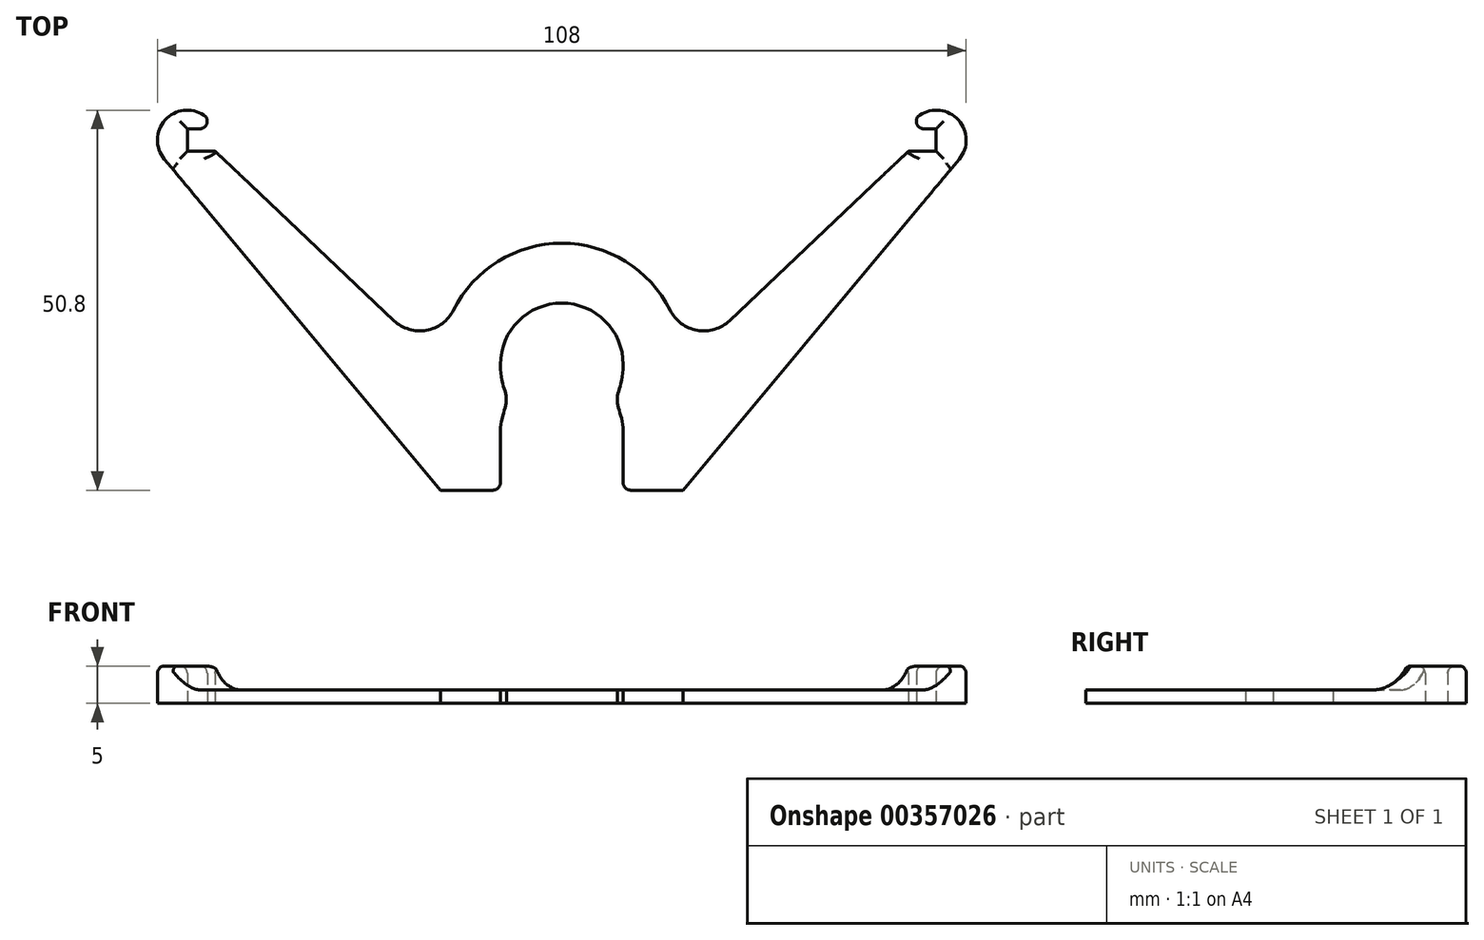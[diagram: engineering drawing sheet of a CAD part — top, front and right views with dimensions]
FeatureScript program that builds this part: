
annotation { "Feature Type Name" : "Feature", "Feature Type Description" : "" }
export const myFeature = defineFeature(function(context is Context, id is Id, definition is map)
    precondition{}
    {
        {
            var Q0;
            Q0=qCreatedBy(makeId("Top.planeOp"),FACE);
            var sketch = newSketch(context, id + "F0", { "sketchPlane" : qUnion([Q0])});
            skArc(sketch, "E0", {"start": v(8.2, 0) * mm, "mid": v(0, 8.2) * mm, "end": v(-8.2, 0) * mm});
            skLineSegment(sketch, "E1.bottom", {"start": v(-8.2, 0) * mm, "end": v(8.2, 0) * mm});
            skLineSegment(sketch, "E1.top", {"start": v(-8.2, -16.8) * mm, "end": v(8.2, -16.8) * mm});
            skLineSegment(sketch, "E1.left", {"start": v(-8.2, 0) * mm, "end": v(-8.2, -16.8) * mm});
            skLineSegment(sketch, "E1.right", {"start": v(8.2, 0) * mm, "end": v(8.2, -16.8) * mm});
            skPoint(sketch, "E1.middle", {"position": v(0, -8.4) * mm});
            skLineSegment(sketch, "E2.0", {"start": v(-7.4, 0) * mm, "end": v(-7.4, -16.8) * mm, "construction": true});
            skFitSpline(sketch, "E3", {"points": [v(-8.2, 0) * mm, v(-7.4, -4.8) * mm, v(-8.2, -8.87) * mm], "startDerivative": vector(0, -14.7) * mm, "endDerivative": vector(0, -10.25) * mm});
            skFitSpline(sketch, "E4.MirrorCS", {"points": [v(8.2, 0) * mm, v(7.4, -4.8) * mm, v(8.2, -8.87) * mm], "startDerivative": vector(0, -14.7) * mm, "endDerivative": vector(0, -10.25) * mm});
            skLineSegment(sketch, "E5.0", {"start": v(-16.2, 0) * mm, "end": v(-16.2, -16.8) * mm});
            skArc(sketch, "E5.1", {"start": v(16.2, 0) * mm, "mid": v(0, 16.2) * mm, "end": v(-16.2, 0) * mm});
            skLineSegment(sketch, "E5.2", {"start": v(16.2, 0) * mm, "end": v(16.2, -16.8) * mm});
            skLineSegment(sketch, "E6", {"start": v(16.2, -16.8) * mm, "end": v(8.2, -16.8) * mm});
            skLineSegment(sketch, "E7", {"start": v(-8.2, -16.8) * mm, "end": v(-16.2, -16.8) * mm});
            skLineSegment(sketch, "E8.bottom", {"start": v(50, 28.5) * mm, "end": v(46.3, 28.5) * mm});
            skLineSegment(sketch, "E8.top", {"start": v(50, 31.5) * mm, "end": v(48.34, 31.5) * mm});
            skLineSegment(sketch, "E8.left", {"start": v(50, 28.5) * mm, "end": v(50, 31.5) * mm});
            skLineSegment(sketch, "E8.right", {"start": v(-50, 28.5) * mm, "end": v(-50, 31.5) * mm});
            skPoint(sketch, "E8.middle", {"position": v(0, 30) * mm});
            skArc(sketch, "E9", {"start": v(46.3, 28.5) * mm, "mid": v(53.82, 28.82) * mm, "end": v(47.79, 33.33) * mm});
            skLineSegment(sketch, "E10", {"start": v(53.07, 27.44) * mm, "end": v(16.2, -16.8) * mm});
            skLineSegment(sketch, "E11.MirrorCS", {"start": v(-53.07, 27.44) * mm, "end": v(-16.2, -16.8) * mm});
            skLineSegment(sketch, "E12.trimOffspring", {"start": v(-46.3, 31.5) * mm, "end": v(-50, 31.5) * mm});
            skPoint(sketch, "E13.visualSharp", {"position": v(46.3, 31.5) * mm});
            skArc(sketch, "E13.filletArc", {"start": v(47.79, 33.33) * mm, "mid": v(47.38, 32.21) * mm, "end": v(48.34, 31.5) * mm});
            skArc(sketch, "E14.MirrorCS", {"start": v(-46.3, 28.5) * mm, "mid": v(-53.82, 28.82) * mm, "end": v(-47.79, 33.33) * mm});
            skArc(sketch, "E15.MirrorCS", {"start": v(-47.79, 33.33) * mm, "mid": v(-47.38, 32.21) * mm, "end": v(-48.34, 31.5) * mm});
            skLineSegment(sketch, "E16", {"start": v(46.3, 28.5) * mm, "end": v(16.2, 0) * mm});
            skLineSegment(sketch, "E17.MirrorCS", {"start": v(-46.3, 28.5) * mm, "end": v(-16.2, 0) * mm});
            skLineSegment(sketch, "E18.trimOffspring", {"start": v(-46.3, 28.5) * mm, "end": v(-50, 28.5) * mm});
            skSolve(sketch);
        }
        {
            var Q0;
            {var subQ6=sQuery(id+"F0.wireOp",EDGE,"E0");Q0=makeQuery(id+"F0.imprint","IMPRINT",FACE,{"disambiguationData":[TD([[makeQuery(id+"F0.imprint","IMPRINT",EDGE,{"derivedFrom":subQ6}),-1.0]])]});}
            var Q1;
            {var subQ0=sQuery(id+"F0.wireOp",EDGE,"E4.MirrorCS");Q1=makeQuery(id+"F0.imprint","IMPRINT",FACE,{"disambiguationData":[TD([[makeQuery(id+"F0.imprint","IMPRINT",EDGE,{"derivedFrom":subQ0}),1.0]])]});}
            var Q2;
            {var subQ0=sQuery(id+"F0.wireOp",EDGE,"E3");Q2=makeQuery(id+"F0.imprint","IMPRINT",FACE,{"disambiguationData":[TD([[makeQuery(id+"F0.imprint","IMPRINT",EDGE,{"derivedFrom":subQ0}),-1.0]])]});}
            var Q3;
            {var subQ0=sQuery(id+"F0.wireOp",EDGE,"E10");Q3=makeQuery(id+"F0.imprint","IMPRINT",FACE,{"disambiguationData":[TD([[makeQuery(id+"F0.imprint","IMPRINT",EDGE,{"derivedFrom":subQ0}),-1.0]])]});}
            var Q4;
            Q4=makeQuery(id+"F0.imprint","IMPRINT",FACE,{"disambiguationData":[TD([[makeQuery(id+"F0.imprint","IMPRINT",EDGE,{"derivedFrom":sQuery(id+"F0.wireOp",EDGE,"E8.top")}),-1.0]])]});
            var Q5;
            {var subQ1=sQuery(id+"F0.wireOp",EDGE,"E8.right");Q5=makeQuery(id+"F0.imprint","IMPRINT",FACE,{"disambiguationData":[TD([[makeQuery(id+"F0.imprint","IMPRINT",EDGE,{"derivedFrom":subQ1}),1.0]])]});}
            var Q6;
            Q6=makeQuery(id+"F0.imprint","IMPRINT",FACE,{"disambiguationData":[TD([[makeQuery(id+"F0.imprint","IMPRINT",EDGE,{"derivedFrom":sQuery(id+"F0.wireOp",EDGE,"E5.0")}),-1.0]])]});
            extrude(context, id + "F1", {"entities" : qUnion([Q0, Q1, Q2, Q3, Q4, Q5, Q6]), "depth" : 1.8 * mm});
        }
        {
            var Q0;
            Q0=makeQuery(id+"F1.opExtrude","SWEPT_EDGE",EDGE,{"disambiguationData":[OSD([sQuery(id+"F0.wireOp",EDGE,"E1.top"),sQuery(id+"F0.wireOp",EDGE,"E1.left"),sQuery(id+"F0.wireOp",EDGE,"E7")])]});
            var Q1;
            Q1=makeQuery(id+"F1.opExtrude","SWEPT_EDGE",EDGE,{"disambiguationData":[OSD([sQuery(id+"F0.wireOp",EDGE,"E1.top"),sQuery(id+"F0.wireOp",EDGE,"E1.right"),sQuery(id+"F0.wireOp",EDGE,"E6")])]});
            fillet(context, id + "F2", {"entities" : qUnion([Q0, Q1]), "radius" : 1 * mm, "tangentPropagation" : true, "allowEdgeOverflow" : false});
        }
        {
            var Q0;
            Q0=makeQuery(id+"F0.imprint","IMPRINT",FACE,{"disambiguationData":[TD([[makeQuery(id+"F0.imprint","IMPRINT",EDGE,{"derivedFrom":sQuery(id+"F0.wireOp",EDGE,"E8.top")}),-1.0]])]});
            var Q1;
            {var subQ1=sQuery(id+"F0.wireOp",EDGE,"E8.right");Q1=makeQuery(id+"F0.imprint","IMPRINT",FACE,{"disambiguationData":[TD([[makeQuery(id+"F0.imprint","IMPRINT",EDGE,{"derivedFrom":subQ1}),1.0]])]});}
            extrude(context, id + "F3", {"entities" : qUnion([Q0, Q1]), "operationType" : NewBodyOperationType.ADD, "depth" : 5 * mm});
        }
        {
            var Q0;
            {var subQ0=sQuery(id+"F0.wireOp",EDGE,"E9");Q0=makeQuery(id+"F3.boolean.opBoolean","INTERSECT",EDGE,{"derivedFrom":[makeQuery(id+"F1.opExtrude","CAP_FACE",FACE,{"disambiguationData":[OSD([sQuery(id+"F0.wireOp",EDGE,"E0"),sQuery(id+"F0.wireOp",EDGE,"E1.left"),sQuery(id+"F0.wireOp",EDGE,"E1.right"),sQuery(id+"F0.wireOp",EDGE,"E3"),sQuery(id+"F0.wireOp",EDGE,"E4.MirrorCS"),sQuery(id+"F0.wireOp",EDGE,"E5.1"),sQuery(id+"F0.wireOp",EDGE,"E6"),sQuery(id+"F0.wireOp",EDGE,"E7"),sQuery(id+"F0.wireOp",EDGE,"E8.bottom"),sQuery(id+"F0.wireOp",EDGE,"E8.top"),sQuery(id+"F0.wireOp",EDGE,"E8.left"),sQuery(id+"F0.wireOp",EDGE,"E8.right"),subQ0,sQuery(id+"F0.wireOp",EDGE,"E10"),sQuery(id+"F0.wireOp",EDGE,"E11.MirrorCS"),sQuery(id+"F0.wireOp",EDGE,"E12.trimOffspring"),sQuery(id+"F0.wireOp",EDGE,"E13.filletArc"),sQuery(id+"F0.wireOp",EDGE,"E14.MirrorCS"),sQuery(id+"F0.wireOp",EDGE,"E15.MirrorCS"),sQuery(id+"F0.wireOp",EDGE,"E16"),sQuery(id+"F0.wireOp",EDGE,"E17.MirrorCS"),sQuery(id+"F0.wireOp",EDGE,"E18.trimOffspring")])],"isStart":false}),makeQuery(id+"F3.opExtrude","SWEPT_FACE",FACE,{"disambiguationData":[OSD([subQ0])]})]});}
            var Q1;
            {var subQ0=sQuery(id+"F0.wireOp",EDGE,"E14.MirrorCS");Q1=makeQuery(id+"F3.boolean.opBoolean","INTERSECT",EDGE,{"derivedFrom":[makeQuery(id+"F1.opExtrude","CAP_FACE",FACE,{"disambiguationData":[OSD([sQuery(id+"F0.wireOp",EDGE,"E0"),sQuery(id+"F0.wireOp",EDGE,"E1.left"),sQuery(id+"F0.wireOp",EDGE,"E1.right"),sQuery(id+"F0.wireOp",EDGE,"E3"),sQuery(id+"F0.wireOp",EDGE,"E4.MirrorCS"),sQuery(id+"F0.wireOp",EDGE,"E5.1"),sQuery(id+"F0.wireOp",EDGE,"E6"),sQuery(id+"F0.wireOp",EDGE,"E7"),sQuery(id+"F0.wireOp",EDGE,"E8.bottom"),sQuery(id+"F0.wireOp",EDGE,"E8.top"),sQuery(id+"F0.wireOp",EDGE,"E8.left"),sQuery(id+"F0.wireOp",EDGE,"E8.right"),sQuery(id+"F0.wireOp",EDGE,"E9"),sQuery(id+"F0.wireOp",EDGE,"E10"),sQuery(id+"F0.wireOp",EDGE,"E11.MirrorCS"),sQuery(id+"F0.wireOp",EDGE,"E12.trimOffspring"),sQuery(id+"F0.wireOp",EDGE,"E13.filletArc"),subQ0,sQuery(id+"F0.wireOp",EDGE,"E15.MirrorCS"),sQuery(id+"F0.wireOp",EDGE,"E16"),sQuery(id+"F0.wireOp",EDGE,"E17.MirrorCS"),sQuery(id+"F0.wireOp",EDGE,"E18.trimOffspring")])],"isStart":false}),makeQuery(id+"F3.opExtrude","SWEPT_FACE",FACE,{"disambiguationData":[OSD([subQ0])]})]});}
            var Q2;
            Q2=makeQuery(id+"F1.opExtrude","SWEPT_EDGE",EDGE,{"disambiguationData":[OSD([sQuery(id+"F0.wireOp",EDGE,"E5.1"),sQuery(id+"F0.wireOp",EDGE,"E5.2"),sQuery(id+"F0.wireOp",EDGE,"E16")])]});
            var Q3;
            Q3=makeQuery(id+"F1.opExtrude","SWEPT_EDGE",EDGE,{"disambiguationData":[OSD([sQuery(id+"F0.wireOp",EDGE,"E5.0"),sQuery(id+"F0.wireOp",EDGE,"E5.1"),sQuery(id+"F0.wireOp",EDGE,"E17.MirrorCS")])]});
            fillet(context, id + "F4", {"entities" : qUnion([Q0, Q1, Q2, Q3]), "radius" : 5 * mm, "tangentPropagation" : true, "allowEdgeOverflow" : false});
        }
        {
            var Q0;
            Q0=makeQuery(id+"F3.opExtrude","CAP_FACE",FACE,{"disambiguationData":[OSD([sQuery(id+"F0.wireOp",EDGE,"E8.bottom"),sQuery(id+"F0.wireOp",EDGE,"E8.top"),sQuery(id+"F0.wireOp",EDGE,"E8.left"),sQuery(id+"F0.wireOp",EDGE,"E9"),sQuery(id+"F0.wireOp",EDGE,"E13.filletArc")])],"isStart":false});
            var Q1;
            {var subQ0=sQuery(id+"F0.wireOp",EDGE,"E8.right");var subQ1=sQuery(id+"F0.wireOp",EDGE,"E8.bottom");var subQ2=sQuery(id+"F0.wireOp",EDGE,"E14.MirrorCS");var subQ3=sQuery(id+"F0.wireOp",EDGE,"E8.left");var subQ4=sQuery(id+"F0.wireOp",EDGE,"E9");Q1=makeQuery(id+"F4.opFillet","BLEND_EDGE",EDGE,{"blendedFrom":[makeQuery(id+"F3.boolean.opBoolean","INTERSECT",EDGE,{"derivedFrom":[makeQuery(id+"F1.opExtrude","CAP_FACE",FACE,{"disambiguationData":[OSD([sQuery(id+"F0.wireOp",EDGE,"E0"),sQuery(id+"F0.wireOp",EDGE,"E1.left"),sQuery(id+"F0.wireOp",EDGE,"E1.right"),sQuery(id+"F0.wireOp",EDGE,"E3"),sQuery(id+"F0.wireOp",EDGE,"E4.MirrorCS"),sQuery(id+"F0.wireOp",EDGE,"E5.0"),sQuery(id+"F0.wireOp",EDGE,"E5.1"),sQuery(id+"F0.wireOp",EDGE,"E5.2"),sQuery(id+"F0.wireOp",EDGE,"E6"),sQuery(id+"F0.wireOp",EDGE,"E7"),subQ1,sQuery(id+"F0.wireOp",EDGE,"E8.top"),subQ3,subQ0,subQ4,sQuery(id+"F0.wireOp",EDGE,"E10"),sQuery(id+"F0.wireOp",EDGE,"E11.MirrorCS"),sQuery(id+"F0.wireOp",EDGE,"E12.trimOffspring"),sQuery(id+"F0.wireOp",EDGE,"E13.filletArc"),subQ2,sQuery(id+"F0.wireOp",EDGE,"E15.MirrorCS")])],"isStart":false}),makeQuery(id+"F3.opExtrude","SWEPT_FACE",FACE,{"disambiguationData":[OSD([subQ4])]})]}),makeQuery(id+"F3.boolean.opBoolean","MERGE",FACE,{"derivedFrom":[makeQuery(id+"F1.opExtrude","SWEPT_FACE",FACE,{"disambiguationData":[OSD([subQ1])]}),makeQuery(id+"F3.opExtrude","SWEPT_FACE",FACE,{"disambiguationData":[OSD([subQ1]),TDD([makeQuery(id+"F0.imprint","IMPRINT",EDGE,{"disambiguationData":[TD([[makeQuery(id+"F0.imprint","INTERSECT",VERTEX,{"derivedFrom":[subQ1,subQ3]}),-1.0]])],"derivedFrom":subQ1})])]}),makeQuery(id+"F3.opExtrude","SWEPT_FACE",FACE,{"disambiguationData":[OSD([subQ1]),TDD([makeQuery(id+"F0.imprint","IMPRINT",EDGE,{"disambiguationData":[TD([[makeQuery(id+"F0.imprint","INTERSECT",VERTEX,{"derivedFrom":[subQ1,subQ0]}),1.0]])],"derivedFrom":subQ1})])]})]})],"blendedInto":[makeQuery(id+"F3.boolean.opBoolean","MERGE",FACE,{"derivedFrom":[makeQuery(id+"F1.opExtrude","SWEPT_FACE",FACE,{"disambiguationData":[OSD([subQ1])]}),makeQuery(id+"F3.opExtrude","SWEPT_FACE",FACE,{"disambiguationData":[OSD([subQ1]),TDD([makeQuery(id+"F0.imprint","IMPRINT",EDGE,{"disambiguationData":[TD([[makeQuery(id+"F0.imprint","INTERSECT",VERTEX,{"derivedFrom":[subQ1,subQ3]}),-1.0]])],"derivedFrom":subQ1})])]}),makeQuery(id+"F3.opExtrude","SWEPT_FACE",FACE,{"disambiguationData":[OSD([subQ1]),TDD([makeQuery(id+"F0.imprint","IMPRINT",EDGE,{"disambiguationData":[TD([[makeQuery(id+"F0.imprint","INTERSECT",VERTEX,{"derivedFrom":[subQ1,subQ0]}),1.0]])],"derivedFrom":subQ1})])]})]})]});}
            var Q2;
            Q2=makeQuery(id+"F3.opExtrude","CAP_EDGE",EDGE,{"disambiguationData":[OSD([sQuery(id+"F0.wireOp",EDGE,"E14.MirrorCS")])],"isStart":false});
            var Q3;
            Q3=makeQuery(id+"F3.opExtrude","CAP_FACE",FACE,{"disambiguationData":[OSD([sQuery(id+"F0.wireOp",EDGE,"E8.bottom"),sQuery(id+"F0.wireOp",EDGE,"E8.right"),sQuery(id+"F0.wireOp",EDGE,"E12.trimOffspring"),sQuery(id+"F0.wireOp",EDGE,"E14.MirrorCS"),sQuery(id+"F0.wireOp",EDGE,"E15.MirrorCS")])],"isStart":false});
            fillet(context, id + "F5", {"entities" : qUnion([Q0, Q1, Q2, Q3]), "radius" : 1 * mm, "tangentPropagation" : true, "allowEdgeOverflow" : false});
        }
    });
